# Revit family: IS_Calla_E2216_BIM_GB
name_source: partatom
category: Plumbing Fixtures
units: mm (PartAtom-declared; Revit-internal decimal feet)

## family parameters
Always vertical = No
Cut with Voids When Loaded = No
OmniClass Number = 23.45.05.14.14
OmniClass Title = Sinks/Lavatories
Part Type = Normal
Room Calculation Point = No
Round Connector Dimension = Use Diameter
Shared = No
Work Plane-Based = No

## types (1)
- E221601 - Calla Basin 60 1Tap Hole
    AreaUnits = Millimeters
    BIMObjectName = IS_IdealStandard_Wallhungwashbasins_Calla_E2216
    BIMobject category = Wash Basins
    BIMobject category code = wash-basins
    BIMobject main category = Sanitary
    BIMobject main category code = sanitary
    BarCode = 5017830556268
    Brand = Ideal Standard
    Brand url = http://www.idealstandard.co.uk
    Color = Gloss White
    ConnectionType = Plumbing
    CurrencyUnit = £
    CurrentRevision = 1
    Date of publishing = 15/12/2021
    Description = Calla Basin 60cm, 1 Tap Hole, Overflow, Glossy White
    DrainSize = 0 mm  [stored 0 ft]
    DurationUnit = Years
    Edition number = 1
    ExpectedLife = 99
    Features = Basin 60cm with 3 hole overflow and 1  tap hole in glossy white finish
    Finish = Gloss White
    GTIN code = https://5017830556268
    Help = https://www.idealstandard.co.uk
    IFC Classification = Sanitary Terminal
    IfcExportAs = IfcSanitaryTerminalType
    IfcExportType = WASHHANDBASIN
    Installation instructions = https://www.idealstandard.co.uk
    InstallationInstructions = https://www.idealstandard.co.uk
    LinearUnits = Millimeter
    MainColor = Gloss White
    MaintenanceInformation = https://www.idealstandard.co.uk
    Manufacturer = Ideal Standard
    Manufacturer name = Ideal Standard
    ManufacturerURL = https://www.idealstandard.co.uk
    Material = Vitreous China
    Material main = Vitreous China
    MaterialThickness = 0 mm  [stored 0 ft]
    Model = E221601
    ModelNumber = E221601
    ModelReference = Calla Basin 60 1Tap Hole
    NBS Reference Code = 45-35-70/369
    NBS Reference Description = Wall hung wash basins
    Name = Wallhungwashbasins_Calla_E2216_IdealStandard
    NettWeight = 18.6
    NominalDepth = 500 mm  [stored 1.64042 ft]
    NominalHeight = 177 mm
    NominalLength = 500 mm  [stored 1.64042 ft]
    NominalWidth = 615 mm
    OmniClass Code = 23-39 29 13 21 19
    OmniClass Description = Surface Water Retention Basin
    OutletConnectionSize = 0 mm  [stored 0 ft]
    Product Guid = 584b21f7-aa51-4738-96b4-d56cff68fc83
    Product SKU = E2216
    Product certification = https://www.idealstandard.co.uk
    Product data url = https://bimobject.com
    Product family = Calla
    Product group = Washbasin
    Product name = Calla Basin 60 1 Tap Hole
    Product url = https://www.idealstandard.co.uk
    ProductInformation = https://www.idealstandard.co.uk
    QR code = http://bimobject.com
    Shape = sculptured
    Size = 615 x 500 x 177 mm
    Space = Internal
    SpareParts = https://fastpart-spares.co.uk
    Technical description = https://www.idealstandard.co.uk
    UNSPSC Code = 301815
    URL = https://www.idealstandard.co.uk
    Uniclass 1.4 Code = L7212
    Uniclass 1.4 Description = Wahsbasins
    Uniclass 2.0 Code = PR-31-79
    Uniclass 2.0 Description = Sink, Wash Basins And Troughs
    Uniclass 2015 Code = Pr_40_20_96_96
    Uniclass 2015 Name = Wall-hung washbasins
    Uniclass2015Code = Pr_40_20_96_96
    Uniclass2015Title = Wall-hung washbasins
    Uniclass2015Version = v1.22
    Version = 1
    VolumeUnits = Litres
    WRASURL = https://www.wrasapprovals.co.uk
    WarrantyDescription = manufacturer warranty
    WarrantyDurationUnit = Years
    Youtube clip = https://www.youtube.com

note: [stored X ft] marks values corroborated as IEEE doubles in the binary element streams (Revit-internal decimal feet)

## geometry (parser evidence)
native form markers: Sweep x2
no freeform markers — native parametric forms only
